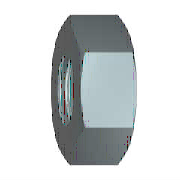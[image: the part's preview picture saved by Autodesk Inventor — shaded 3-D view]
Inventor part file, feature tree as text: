
AUTODESK INVENTOR PART (.ipt)
format: ipt  version: 2015 (Build 190159000, 159)  size: 171,520 bytes
history: native  units: mm (DEFAULTED — no unit token found)
features: sketch x2, chamfer x2, hole x1, other x1, plane x1
ambient origin geometry x7: Origin, YZ Plane, XZ Plane, X Axis, Y Axis, Z Axis, Center Point
bodies: Solid1 (feature_tree), Body (feature_tree)
feature tree (7):
  hole  "Thread"  [1 undecoded]
  sketch  "Sketch3"  dims[d2=0.0mm d3=42.587mm d4=6.0mm d5=4.0mm d6=2.0mm d7=14.3117mm d8=8.0mm d9=20.594885mm d10=2.706329mm d11=30.0deg d12=2.706329mm d13=30.0deg d15=0.0mm d17=80.0mm d18=30.0deg d19=73.7mm d20=1.0mm d21=90.0deg d22=90.0deg d23=0.0mm d24=2.706329mm d25=2.706329mm d26=0.0mm d27=0.0mm]
  chamfer  "Chamfer3"  Distance=2.706329mm
  chamfer  "Chamfer4"  Angle=30.0deg  [1 undecoded]
  other  "Work Axis1"
  plane  "Work Plane1"
  sketch  "Sketch1"  dims[d0=92.376043mm d1=48.0mm]
note: 2 required parameter values undecoded (feature->parameter linkage not recoverable at this tier; creation-order binding heuristic only, values carry confidence <= 0.55)
